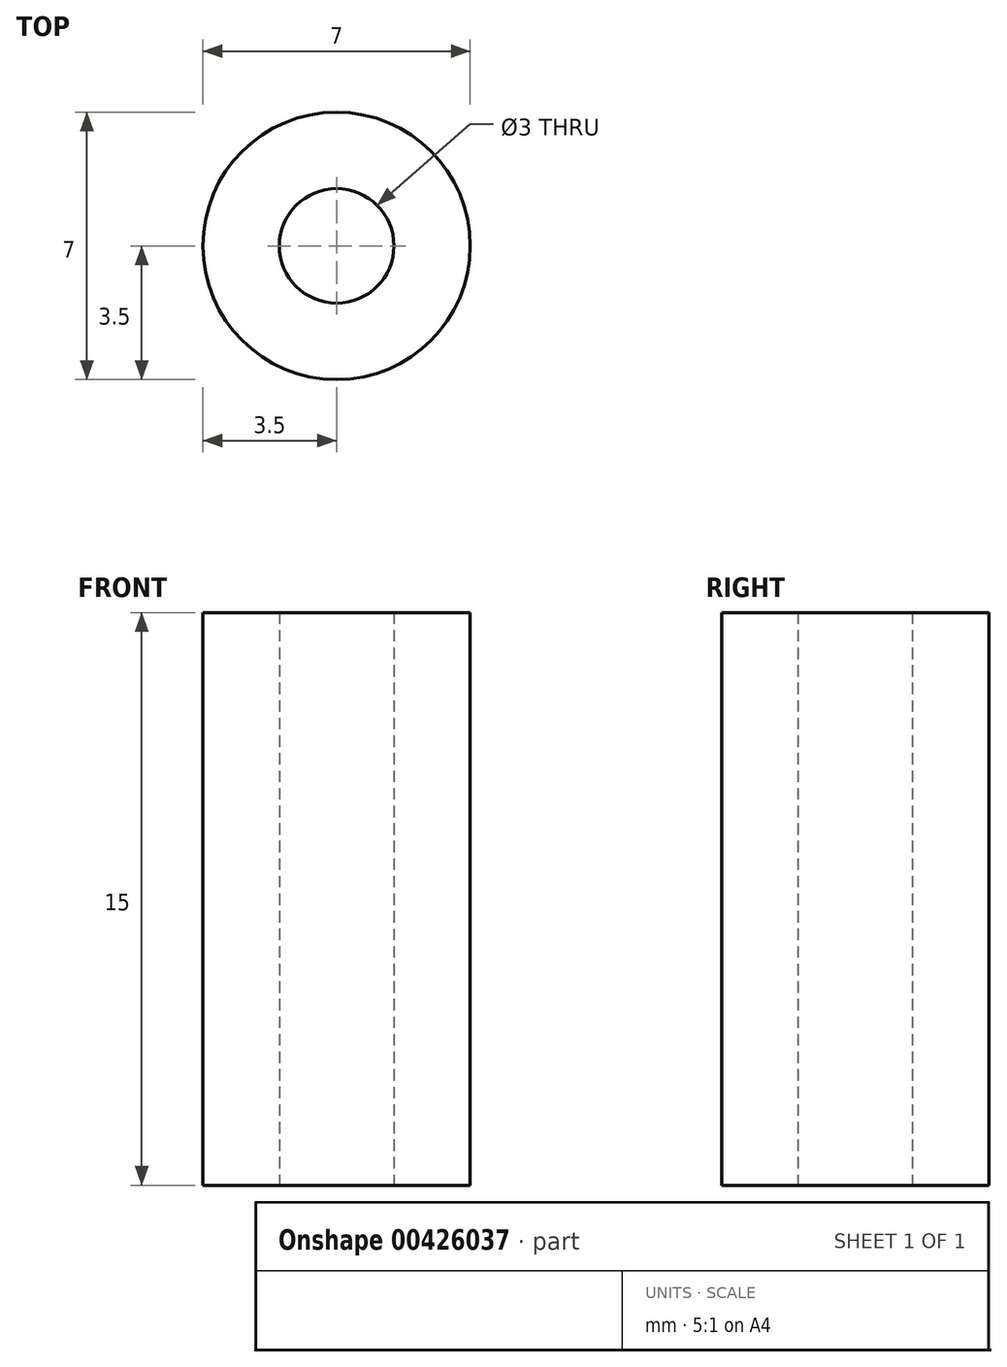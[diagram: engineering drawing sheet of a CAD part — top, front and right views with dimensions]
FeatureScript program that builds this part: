
annotation { "Feature Type Name" : "Feature", "Feature Type Description" : "" }
export const myFeature = defineFeature(function(context is Context, id is Id, definition is map)
    precondition{}
    {
        {
            var Q0;
            Q0=qCreatedBy(makeId("Top.planeOp"),FACE);
            var sketch = newSketch(context, id + "F0", { "sketchPlane" : qUnion([Q0])});
            skCircle(sketch, "E0", {"center": v(0, 0) * mm, "radius": 3.5 * mm});
            skCircle(sketch, "E1", {"center": v(0, 0) * mm, "radius": 1.5 * mm});
            skSolve(sketch);
        }
        {
            var Q0;
            Q0=makeQuery(id+"F0.imprint","IMPRINT",FACE,{"disambiguationData":[TD([[makeQuery(id+"F0.imprint","IMPRINT",EDGE,{"derivedFrom":sQuery(id+"F0.wireOp",EDGE,"E0")}),1.0]])]});
            extrude(context, id + "F1", {"entities" : qUnion([Q0]), "depth" : 15 * mm});
        }
    });
